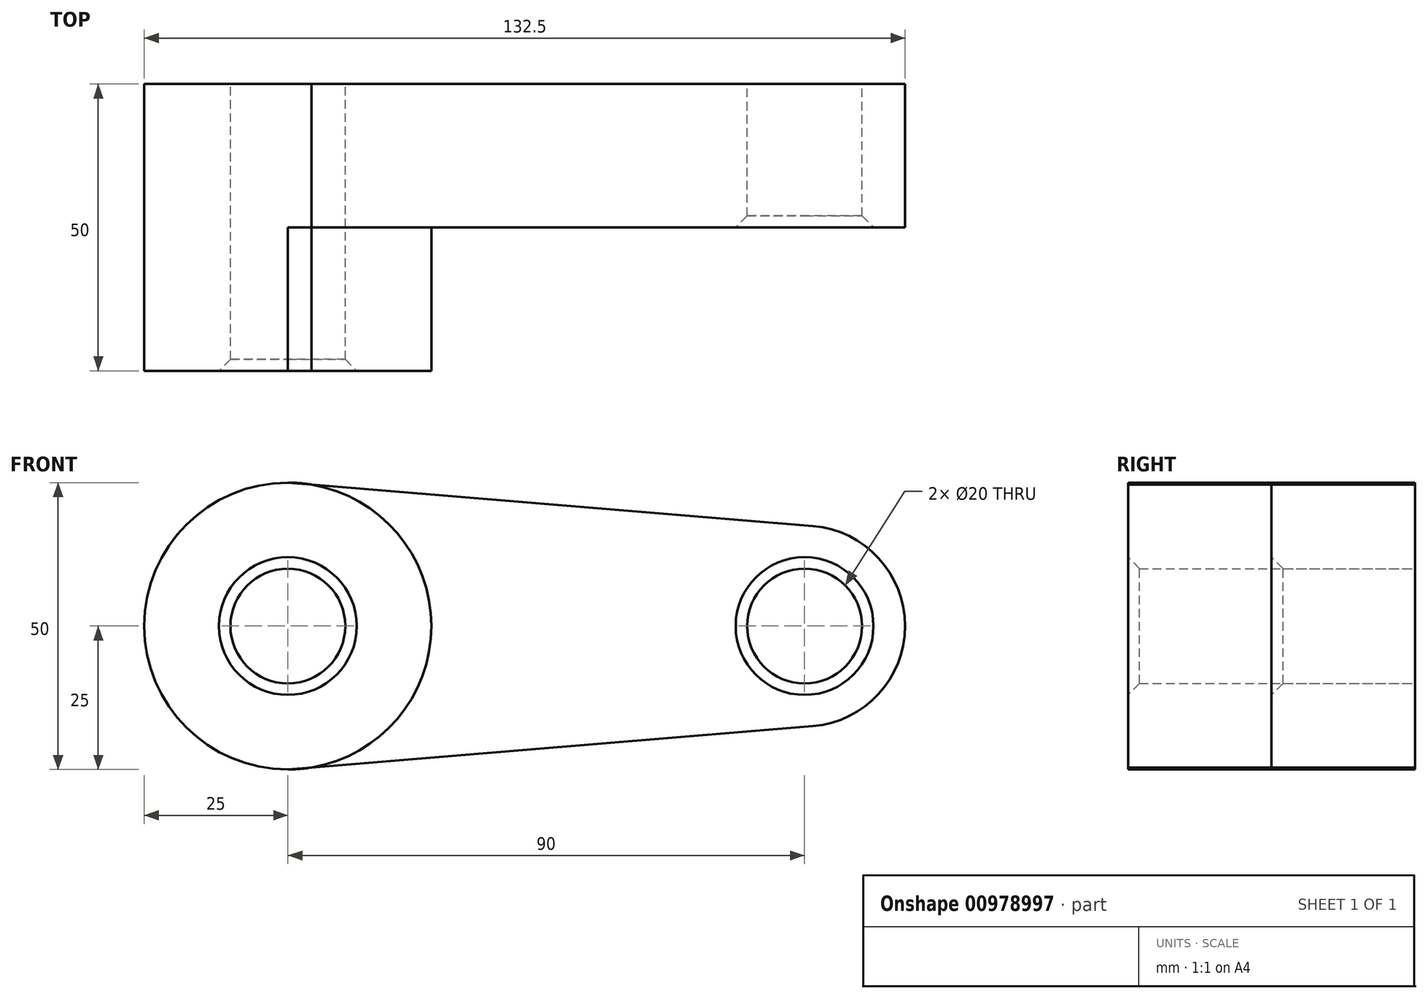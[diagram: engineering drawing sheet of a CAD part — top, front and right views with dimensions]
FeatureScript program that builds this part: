
annotation { "Feature Type Name" : "Feature", "Feature Type Description" : "" }
export const myFeature = defineFeature(function(context is Context, id is Id, definition is map)
    precondition{}
    {
        {
            var Q0;
            Q0=qCreatedBy(makeId("Front.planeOp"),FACE);
            var sketch = newSketch(context, id + "F0", { "sketchPlane" : qUnion([Q0])});
            skCircle(sketch, "E0", {"center": v(0, 0) * mm, "radius": 25 * mm});
            skCircle(sketch, "E1", {"center": v(90, 0) * mm, "radius": 17.5 * mm});
            skLineSegment(sketch, "E2", {"start": v(0, 25) * mm, "end": v(91.44, 17.44) * mm});
            skLineSegment(sketch, "E3", {"start": v(0, -25) * mm, "end": v(91.44, -17.44) * mm});
            skCircle(sketch, "E4", {"center": v(0, 0) * mm, "radius": 10 * mm});
            skCircle(sketch, "E5", {"center": v(90, 0) * mm, "radius": 10 * mm});
            skSolve(sketch);
        }
        {
            var Q0;
            Q0 = qSketchRegion(id + "F0", true);
            extrude(context, id + "F1", {"entities" : qUnion([Q0]), "depth" : 25 * mm, "offsetDistance" : 25 * mm});
        }
        {
            var Q0;
            Q0=makeQuery(id+"F0.imprint","IMPRINT",FACE,{"disambiguationData":[TD([[makeQuery(id+"F0.imprint","IMPRINT",EDGE,{"derivedFrom":sQuery(id+"F0.wireOp",EDGE,"E4")}),-1.0]])]});
            extrude(context, id + "F2", {"entities" : qUnion([Q0]), "operationType" : NewBodyOperationType.ADD, "depth" : 50 * mm, "offsetDistance" : 25 * mm});
        }
        {
            var Q0;
            Q0=makeQuery(id+"F2.opExtrude","CAP_EDGE",EDGE,{"disambiguationData":[OSD([sQuery(id+"F0.wireOp",EDGE,"E4")])],"isStart":false});
            var Q1;
            {var subQ0=sQuery(id+"F0.wireOp",EDGE,"E0");Q1=makeQuery(id+"F2.opExtrude","CAP_EDGE",EDGE,{"disambiguationData":[OSD([subQ0]),TDD([makeQuery(id+"F0.imprint","IMPRINT",EDGE,{"disambiguationData":[TD([[makeQuery(id+"F0.imprint","INTERSECT",VERTEX,{"disambiguationData":[OD(0.0)],"derivedFrom":[subQ0,sQuery(id+"F0.wireOp",EDGE,"E2")]}),-1.0]])],"derivedFrom":subQ0})])],"isStart":false});}
            var Q2;
            Q2=makeQuery(id+"F1.opExtrude","CAP_EDGE",EDGE,{"disambiguationData":[OSD([sQuery(id+"F0.wireOp",EDGE,"E5")])],"isStart":false});
            chamfer(context, id + "F3", {"entities" : qUnion([Q0, Q1, Q2]), "width" : 2 * mm, "tangentPropagation" : true});
        }
    });
